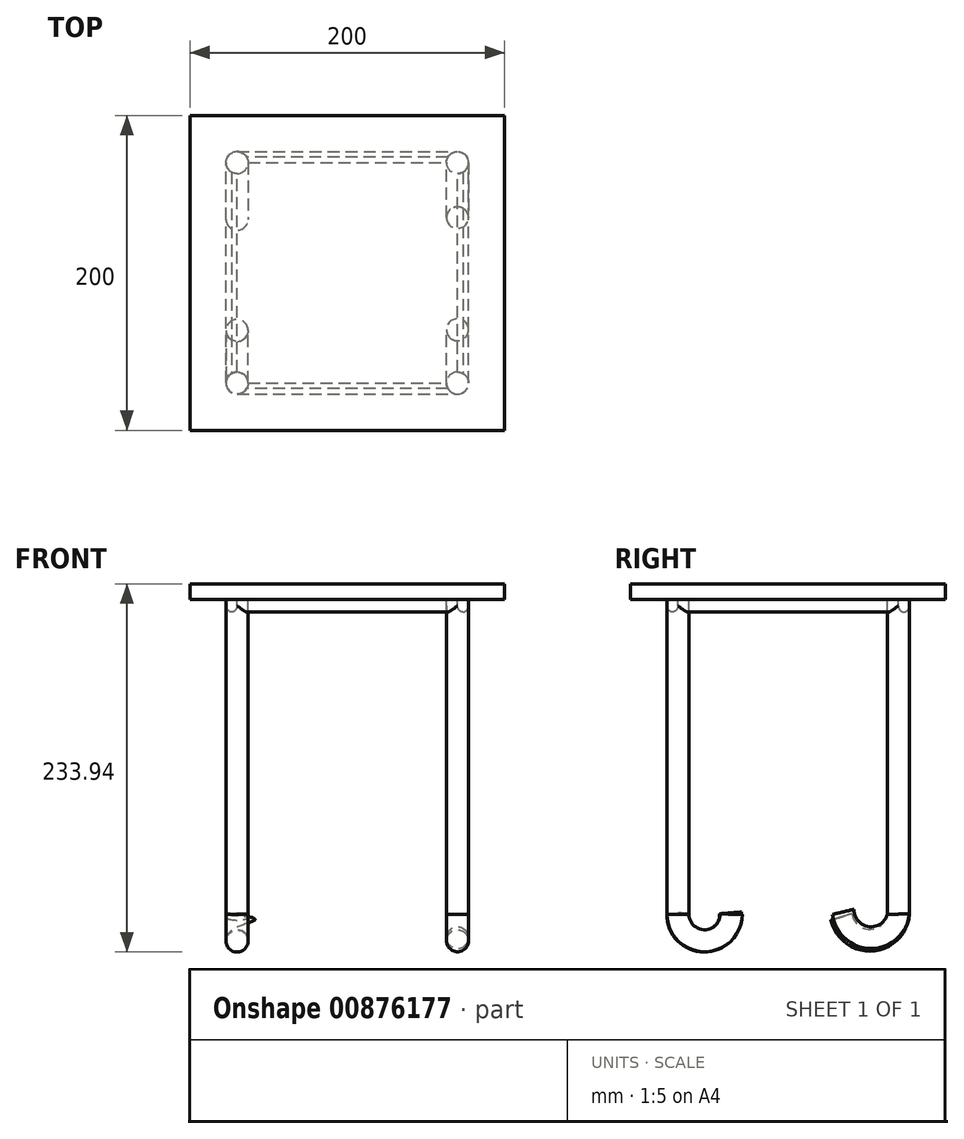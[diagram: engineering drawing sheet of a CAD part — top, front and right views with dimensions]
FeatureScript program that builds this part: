
annotation { "Feature Type Name" : "Feature", "Feature Type Description" : "" }
export const myFeature = defineFeature(function(context is Context, id is Id, definition is map)
    precondition{}
    {
        {
            var Q0;
            Q0=qCreatedBy(makeId("Top.planeOp"),FACE);
            var sketch = newSketch(context, id + "F0", { "sketchPlane" : qUnion([Q0])});
            skLineSegment(sketch, "E0.bottom", {"start": v(100, -100) * mm, "end": v(-100, -100) * mm});
            skLineSegment(sketch, "E0.top", {"start": v(100, 100) * mm, "end": v(-100, 100) * mm});
            skLineSegment(sketch, "E0.left", {"start": v(100, -100) * mm, "end": v(100, 100) * mm});
            skLineSegment(sketch, "E0.right", {"start": v(-100, -100) * mm, "end": v(-100, 100) * mm});
            skPoint(sketch, "E0.middle", {"position": v(0, 0) * mm});
            skSolve(sketch);
        }
        {
            var Q0;
            Q0=makeQuery(id+"F0.imprint","IMPRINT",FACE,{"disambiguationData":[TD([[makeQuery(id+"F0.imprint","IMPRINT",EDGE,{"derivedFrom":sQuery(id+"F0.wireOp",EDGE,"E0.bottom")}),-1.0]])]});
            extrude(context, id + "F1", {"entities" : qUnion([Q0]), "depth" : 10 * mm, "offsetDistance" : 25 * mm});
        }
        {
            var Q0;
            Q0=makeQuery(id+"F1.opExtrude","CAP_FACE",FACE,{"disambiguationData":[OSD([sQuery(id+"F0.wireOp",EDGE,"E0.bottom"),sQuery(id+"F0.wireOp",EDGE,"E0.top"),sQuery(id+"F0.wireOp",EDGE,"E0.left"),sQuery(id+"F0.wireOp",EDGE,"E0.right")])],"isStart":true});
            var sketch = newSketch(context, id + "F2", { "sketchPlane" : qUnion([Q0])});
            skLineSegment(sketch, "E1.bottom", {"start": v(-70, 70) * mm, "end": v(70, 70) * mm});
            skLineSegment(sketch, "E1.top", {"start": v(-70, -70) * mm, "end": v(70, -70) * mm});
            skLineSegment(sketch, "E1.left", {"start": v(-70, 70) * mm, "end": v(-70, -70) * mm});
            skLineSegment(sketch, "E1.right", {"start": v(70, 70) * mm, "end": v(70, -70) * mm});
            skPoint(sketch, "E1.middle", {"position": v(0, 0) * mm});
            skSolve(sketch);
        }
        {
            var Q0;
            Q0=makeQuery(id+"F2.imprint","IMPRINT",FACE,{"disambiguationData":[TD([[makeQuery(id+"F2.imprint","IMPRINT",EDGE,{"derivedFrom":sQuery(id+"F2.wireOp",EDGE,"E1.bottom")}),1.0]])]});
            var sketch = newSketch(context, id + "F3", { "sketchPlane" : qUnion([Q0])});
            skCircle(sketch, "E2", {"center": v(70, -70) * mm, "radius": 7 * mm});
            skCircle(sketch, "E3", {"center": v(-70, -70) * mm, "radius": 7 * mm});
            skCircle(sketch, "E4", {"center": v(-70, 70) * mm, "radius": 7 * mm});
            skCircle(sketch, "E5", {"center": v(70, 70) * mm, "radius": 7 * mm});
            skSolve(sketch);
        }
        {
            var Q0;
            {var subQ0=sQuery(id+"F3.wireOp",EDGE,"E2");var subQ1=makeQuery(id+"F2.imprint","IMPRINT",EDGE,{"derivedFrom":sQuery(id+"F2.wireOp",EDGE,"E1.top")});var subQ2=makeQuery(id+"F3.imprint","INTERSECT",VERTEX,{"derivedFrom":[subQ1,subQ0]});Q0=makeQuery(id+"F3.imprint","IMPRINT",FACE,{"disambiguationData":[TD([[makeQuery(id+"F3.imprint","IMPRINT",EDGE,{"disambiguationData":[TD([[subQ2,-1.0]])],"derivedFrom":subQ0}),1.0]])]});}
            var Q1;
            {var subQ0=sQuery(id+"F3.wireOp",EDGE,"E2");var subQ1=makeQuery(id+"F2.imprint","IMPRINT",EDGE,{"derivedFrom":sQuery(id+"F2.wireOp",EDGE,"E1.top")});var subQ2=makeQuery(id+"F3.imprint","INTERSECT",VERTEX,{"derivedFrom":[subQ1,subQ0]});Q1=makeQuery(id+"F3.imprint","IMPRINT",FACE,{"disambiguationData":[TD([[makeQuery(id+"F3.imprint","IMPRINT",EDGE,{"disambiguationData":[TD([[subQ2,1.0]])],"derivedFrom":subQ0}),1.0]])]});}
            var Q2;
            {var subQ0=sQuery(id+"F3.wireOp",EDGE,"E3");var subQ1=makeQuery(id+"F2.imprint","IMPRINT",EDGE,{"derivedFrom":sQuery(id+"F2.wireOp",EDGE,"E1.top")});var subQ2=makeQuery(id+"F3.imprint","INTERSECT",VERTEX,{"derivedFrom":[subQ1,subQ0]});Q2=makeQuery(id+"F3.imprint","IMPRINT",FACE,{"disambiguationData":[TD([[makeQuery(id+"F3.imprint","IMPRINT",EDGE,{"disambiguationData":[TD([[subQ2,1.0]])],"derivedFrom":subQ0}),1.0]])]});}
            var Q3;
            {var subQ0=sQuery(id+"F3.wireOp",EDGE,"E3");var subQ1=makeQuery(id+"F2.imprint","IMPRINT",EDGE,{"derivedFrom":sQuery(id+"F2.wireOp",EDGE,"E1.top")});var subQ2=makeQuery(id+"F3.imprint","INTERSECT",VERTEX,{"derivedFrom":[subQ1,subQ0]});Q3=makeQuery(id+"F3.imprint","IMPRINT",FACE,{"disambiguationData":[TD([[makeQuery(id+"F3.imprint","IMPRINT",EDGE,{"disambiguationData":[TD([[subQ2,-1.0]])],"derivedFrom":subQ0}),1.0]])]});}
            var Q4;
            {var subQ0=sQuery(id+"F3.wireOp",EDGE,"E4");var subQ1=makeQuery(id+"F2.imprint","IMPRINT",EDGE,{"derivedFrom":sQuery(id+"F2.wireOp",EDGE,"E1.bottom")});var subQ2=makeQuery(id+"F3.imprint","INTERSECT",VERTEX,{"derivedFrom":[subQ1,subQ0]});Q4=makeQuery(id+"F3.imprint","IMPRINT",FACE,{"disambiguationData":[TD([[makeQuery(id+"F3.imprint","IMPRINT",EDGE,{"disambiguationData":[TD([[subQ2,-1.0]])],"derivedFrom":subQ0}),1.0]])]});}
            var Q5;
            {var subQ0=sQuery(id+"F3.wireOp",EDGE,"E4");var subQ1=makeQuery(id+"F2.imprint","IMPRINT",EDGE,{"derivedFrom":sQuery(id+"F2.wireOp",EDGE,"E1.bottom")});var subQ2=makeQuery(id+"F3.imprint","INTERSECT",VERTEX,{"derivedFrom":[subQ1,subQ0]});Q5=makeQuery(id+"F3.imprint","IMPRINT",FACE,{"disambiguationData":[TD([[makeQuery(id+"F3.imprint","IMPRINT",EDGE,{"disambiguationData":[TD([[subQ2,1.0]])],"derivedFrom":subQ0}),1.0]])]});}
            var Q6;
            {var subQ0=sQuery(id+"F3.wireOp",EDGE,"E5");var subQ1=makeQuery(id+"F2.imprint","IMPRINT",EDGE,{"derivedFrom":sQuery(id+"F2.wireOp",EDGE,"E1.bottom")});var subQ2=makeQuery(id+"F3.imprint","INTERSECT",VERTEX,{"derivedFrom":[subQ1,subQ0]});Q6=makeQuery(id+"F3.imprint","IMPRINT",FACE,{"disambiguationData":[TD([[makeQuery(id+"F3.imprint","IMPRINT",EDGE,{"disambiguationData":[TD([[subQ2,1.0]])],"derivedFrom":subQ0}),1.0]])]});}
            var Q7;
            {var subQ0=sQuery(id+"F3.wireOp",EDGE,"E5");var subQ1=makeQuery(id+"F2.imprint","IMPRINT",EDGE,{"derivedFrom":sQuery(id+"F2.wireOp",EDGE,"E1.bottom")});var subQ2=makeQuery(id+"F3.imprint","INTERSECT",VERTEX,{"derivedFrom":[subQ1,subQ0]});Q7=makeQuery(id+"F3.imprint","IMPRINT",FACE,{"disambiguationData":[TD([[makeQuery(id+"F3.imprint","IMPRINT",EDGE,{"disambiguationData":[TD([[subQ2,-1.0]])],"derivedFrom":subQ0}),1.0]])]});}
            extrude(context, id + "F4", {"entities" : qUnion([Q0, Q1, Q2, Q3, Q4, Q5, Q6, Q7]), "operationType" : NewBodyOperationType.ADD, "depth" : 200 * mm, "offsetDistance" : 25 * mm});
        }
        {
            var Q0;
            Q0=makeQuery(id+"F2.imprint","IMPRINT",FACE,{"disambiguationData":[TD([[makeQuery(id+"F2.imprint","IMPRINT",EDGE,{"derivedFrom":sQuery(id+"F2.wireOp",EDGE,"E1.bottom")}),1.0]])]});
            var sketch = newSketch(context, id + "F5", { "sketchPlane" : qUnion([Q0])});
            skLineSegment(sketch, "E6.bottom", {"start": v(-73, 73) * mm, "end": v(73, 73) * mm});
            skLineSegment(sketch, "E6.top", {"start": v(-73, -73) * mm, "end": v(73, -73) * mm});
            skLineSegment(sketch, "E6.left", {"start": v(-73, 73) * mm, "end": v(-73, -73) * mm});
            skLineSegment(sketch, "E6.right", {"start": v(73, 73) * mm, "end": v(73, -73) * mm});
            skPoint(sketch, "E6.middle", {"position": v(0, 0) * mm});
            skSolve(sketch);
        }
        {
            var Q0;
            Q0=makeQuery(id+"F3.imprint","IMPRINT",FACE,{"disambiguationData":[TD([[makeQuery(id+"F3.imprint","IMPRINT",EDGE,{"derivedFrom":makeQuery(id+"F2.imprint","IMPRINT",EDGE,{"derivedFrom":makeQuery(id+"F1.opExtrude","CAP_EDGE",EDGE,{"disambiguationData":[OSD([sQuery(id+"F0.wireOp",EDGE,"E0.bottom")])],"isStart":true})})}),1.0]])]});
            var sketch = newSketch(context, id + "F6", { "sketchPlane" : qUnion([Q0])});
            skLineSegment(sketch, "E7.bottom", {"start": v(-77, 77) * mm, "end": v(77, 77) * mm});
            skLineSegment(sketch, "E7.top", {"start": v(-77, -77) * mm, "end": v(77, -77) * mm});
            skLineSegment(sketch, "E7.left", {"start": v(-77, 77) * mm, "end": v(-77, -77) * mm});
            skLineSegment(sketch, "E7.right", {"start": v(77, 77) * mm, "end": v(77, -77) * mm});
            skPoint(sketch, "E7.middle", {"position": v(0, 0) * mm});
            skSolve(sketch);
        }
        {
            var Q0;
            {var subQ2=makeQuery(id+"F2.imprint","IMPRINT",EDGE,{"derivedFrom":sQuery(id+"F2.wireOp",EDGE,"E1.right")});var subQ6=sQuery(id+"F3.wireOp",EDGE,"E2");var subQ7=makeQuery(id+"F3.imprint","INTERSECT",VERTEX,{"derivedFrom":[subQ2,subQ6]});var subQ10=makeQuery(id+"F3.imprint","IMPRINT",EDGE,{"disambiguationData":[TD([[subQ7,1.0]])],"derivedFrom":subQ2});Q0=makeQuery(id+"F6.imprint","IMPRINT",FACE,{"disambiguationData":[TD([[makeQuery(id+"F6.imprint","IMPRINT",EDGE,{"derivedFrom":subQ10}),1.0]])]});}
            var Q1;
            {var subQ2=makeQuery(id+"F2.imprint","IMPRINT",EDGE,{"derivedFrom":sQuery(id+"F2.wireOp",EDGE,"E1.left")});var subQ6=sQuery(id+"F3.wireOp",EDGE,"E3");var subQ7=makeQuery(id+"F3.imprint","INTERSECT",VERTEX,{"derivedFrom":[subQ2,subQ6]});var subQ10=makeQuery(id+"F3.imprint","IMPRINT",EDGE,{"disambiguationData":[TD([[subQ7,1.0]])],"derivedFrom":subQ2});Q1=makeQuery(id+"F6.imprint","IMPRINT",FACE,{"disambiguationData":[TD([[makeQuery(id+"F6.imprint","IMPRINT",EDGE,{"derivedFrom":subQ10}),-1.0]])]});}
            var Q2;
            Q2=makeQuery(id+"F5.imprint","IMPRINT",FACE,{"disambiguationData":[TD([[makeQuery(id+"F5.imprint","IMPRINT",EDGE,{"derivedFrom":sQuery(id+"F5.wireOp",EDGE,"E6.bottom")}),-1.0]])]});
            var Q3;
            {var subQ1=sQuery(id+"F3.wireOp",EDGE,"E4");var subQ2=makeQuery(id+"F2.imprint","IMPRINT",EDGE,{"derivedFrom":sQuery(id+"F2.wireOp",EDGE,"E1.bottom")});var subQ3=makeQuery(id+"F3.imprint","INTERSECT",VERTEX,{"derivedFrom":[subQ2,subQ1]});var subQ10=makeQuery(id+"F3.imprint","IMPRINT",EDGE,{"disambiguationData":[TD([[subQ3,-1.0]])],"derivedFrom":subQ2});Q3=makeQuery(id+"F6.imprint","IMPRINT",FACE,{"disambiguationData":[TD([[makeQuery(id+"F6.imprint","IMPRINT",EDGE,{"derivedFrom":subQ10}),1.0]])]});}
            var Q4;
            {var subQ2=makeQuery(id+"F2.imprint","IMPRINT",EDGE,{"derivedFrom":sQuery(id+"F2.wireOp",EDGE,"E1.top")});var subQ6=sQuery(id+"F3.wireOp",EDGE,"E2");var subQ7=makeQuery(id+"F3.imprint","INTERSECT",VERTEX,{"derivedFrom":[subQ2,subQ6]});var subQ10=makeQuery(id+"F3.imprint","IMPRINT",EDGE,{"disambiguationData":[TD([[subQ7,1.0]])],"derivedFrom":subQ2});Q4=makeQuery(id+"F6.imprint","IMPRINT",FACE,{"disambiguationData":[TD([[makeQuery(id+"F6.imprint","IMPRINT",EDGE,{"derivedFrom":subQ10}),-1.0]])]});}
            extrude(context, id + "F7", {"entities" : qUnion([Q0, Q1, Q2, Q3, Q4]), "operationType" : NewBodyOperationType.ADD, "depth" : 8 * mm, "offsetDistance" : 25 * mm});
        }
        {
            var Q0;
            Q0=makeQuery(id+"F7.opExtrude","CAP_EDGE",EDGE,{"disambiguationData":[OSD([sQuery(id+"F6.wireOp",EDGE,"E7.top")])],"isStart":false});
            var Q1;
            {var subQ0=sQuery(id+"F2.wireOp",EDGE,"E1.top");Q1=makeQuery(id+"F7.opExtrude","CAP_EDGE",EDGE,{"disambiguationData":[OSD([subQ0]),TDD([makeQuery(id+"F5.imprint","IMPRINT",EDGE,{"derivedFrom":makeQuery(id+"F2.imprint","IMPRINT",EDGE,{"derivedFrom":subQ0})})])],"isStart":false});}
            var Q2;
            Q2=makeQuery(id+"F7.opExtrude","CAP_EDGE",EDGE,{"disambiguationData":[OSD([sQuery(id+"F6.wireOp",EDGE,"E7.left")])],"isStart":false});
            var Q3;
            {var subQ0=sQuery(id+"F2.wireOp",EDGE,"E1.left");Q3=makeQuery(id+"F7.opExtrude","CAP_EDGE",EDGE,{"disambiguationData":[OSD([subQ0]),TDD([makeQuery(id+"F5.imprint","IMPRINT",EDGE,{"derivedFrom":makeQuery(id+"F2.imprint","IMPRINT",EDGE,{"derivedFrom":subQ0})})])],"isStart":false});}
            var Q4;
            {var subQ0=sQuery(id+"F2.wireOp",EDGE,"E1.bottom");Q4=makeQuery(id+"F7.opExtrude","CAP_EDGE",EDGE,{"disambiguationData":[OSD([subQ0]),TDD([makeQuery(id+"F5.imprint","IMPRINT",EDGE,{"derivedFrom":makeQuery(id+"F2.imprint","IMPRINT",EDGE,{"derivedFrom":subQ0})})])],"isStart":false});}
            var Q5;
            Q5=makeQuery(id+"F7.opExtrude","CAP_EDGE",EDGE,{"disambiguationData":[OSD([sQuery(id+"F6.wireOp",EDGE,"E7.bottom")])],"isStart":false});
            var Q6;
            {var subQ0=sQuery(id+"F2.wireOp",EDGE,"E1.right");Q6=makeQuery(id+"F7.opExtrude","CAP_EDGE",EDGE,{"disambiguationData":[OSD([subQ0]),TDD([makeQuery(id+"F5.imprint","IMPRINT",EDGE,{"derivedFrom":makeQuery(id+"F2.imprint","IMPRINT",EDGE,{"derivedFrom":subQ0})})])],"isStart":false});}
            var Q7;
            Q7=makeQuery(id+"F7.opExtrude","CAP_EDGE",EDGE,{"disambiguationData":[OSD([sQuery(id+"F6.wireOp",EDGE,"E7.right")])],"isStart":false});
            fillet(context, id + "F8", {"entities" : qUnion([Q0, Q1, Q2, Q3, Q4, Q5, Q6, Q7]), "radius" : 4 * mm, "tangentPropagation" : true, "allowEdgeOverflow" : false});
        }
        {
            var Q0;
            Q0=qCreatedBy(makeId("Right.planeOp"),FACE);
            cPlane(context, id + "F9", {"entities" : qUnion([Q0]), "cplaneType" : CPlaneType.OFFSET, "offset" : 70 * mm, "width" : 150 * mm, "height" : 150 * mm});
        }
        {
            var Q0;
            Q0=qCreatedBy(makeId("Right.planeOp"),FACE);
            cPlane(context, id + "F10", {"entities" : qUnion([Q0]), "cplaneType" : CPlaneType.OFFSET, "offset" : 70 * mm, "oppositeDirection" : true, "width" : 150 * mm, "height" : 150 * mm});
        }
        {
            var Q0;
            Q0=qCreatedBy(id+"F9.planeOp",FACE);
            var sketch = newSketch(context, id + "F11", { "sketchPlane" : qUnion([Q0])});
            skArc(sketch, "E8", {"start": v(-69.95, -199.69) * mm, "mid": v(-53.15, -216.66) * mm, "end": v(-36.18, -199.86) * mm});
            skSolve(sketch);
        }
        {
            var Q0;
            Q0=makeQuery(id+"F4.opExtrude","CAP_FACE",FACE,{"disambiguationData":[OSD([sQuery(id+"F3.wireOp",EDGE,"E5")])],"isStart":false});
            var Q1;
            Q1=sQuery(id+"F11.wireOp",EDGE,"E8");
            sweep(context, id + "F12", {"operationType" : NewBodyOperationType.ADD, "profiles" : qUnion([Q0]), "path" : qUnion([Q1])});
        }
        {
            var Q0;
            Q0=qCreatedBy(id+"F10.planeOp",FACE);
            var sketch = newSketch(context, id + "F13", { "sketchPlane" : qUnion([Q0])});
            skArc(sketch, "E9", {"start": v(34.04, -201.56) * mm, "mid": v(52.75, -216.18) * mm, "end": v(69.84, -199.7) * mm});
            skSolve(sketch);
        }
        {
            var Q0;
            Q0=makeQuery(id+"F4.opExtrude","CAP_FACE",FACE,{"disambiguationData":[OSD([sQuery(id+"F3.wireOp",EDGE,"E3")])],"isStart":false});
            var Q1;
            Q1=sQuery(id+"F13.wireOp",EDGE,"E9");
            sweep(context, id + "F14", {"operationType" : NewBodyOperationType.ADD, "profiles" : qUnion([Q0]), "path" : qUnion([Q1])});
        }
        {
            var Q0;
            Q0=qCreatedBy(id+"F9.planeOp",FACE);
            var sketch = newSketch(context, id + "F15", { "sketchPlane" : qUnion([Q0])});
            skArc(sketch, "E10", {"start": v(33.4, -198.75) * mm, "mid": v(52.13, -216.42) * mm, "end": v(71.75, -199.77) * mm});
            skSolve(sketch);
        }
        {
            var Q0;
            Q0=makeQuery(id+"F4.opExtrude","CAP_FACE",FACE,{"disambiguationData":[OSD([sQuery(id+"F3.wireOp",EDGE,"E2")])],"isStart":false});
            var Q1;
            Q1=sQuery(id+"F15.wireOp",EDGE,"E10");
            sweep(context, id + "F16", {"operationType" : NewBodyOperationType.ADD, "profiles" : qUnion([Q0]), "path" : qUnion([Q1])});
        }
        {
            var Q0;
            Q0=qCreatedBy(id+"F10.planeOp",FACE);
            var sketch = newSketch(context, id + "F17", { "sketchPlane" : qUnion([Q0])});
            skArc(sketch, "E11", {"start": v(-70.22, -199.03) * mm, "mid": v(-53.28, -217.2) * mm, "end": v(-36.33, -199.03) * mm});
            skSolve(sketch);
        }
        {
            var Q0;
            Q0=makeQuery(id+"F4.opExtrude","CAP_FACE",FACE,{"disambiguationData":[OSD([sQuery(id+"F3.wireOp",EDGE,"E4")])],"isStart":false});
            var Q1;
            Q1=sQuery(id+"F17.wireOp",EDGE,"E11");
            sweep(context, id + "F18", {"operationType" : NewBodyOperationType.ADD, "profiles" : qUnion([Q0]), "path" : qUnion([Q1])});
        }
    });
